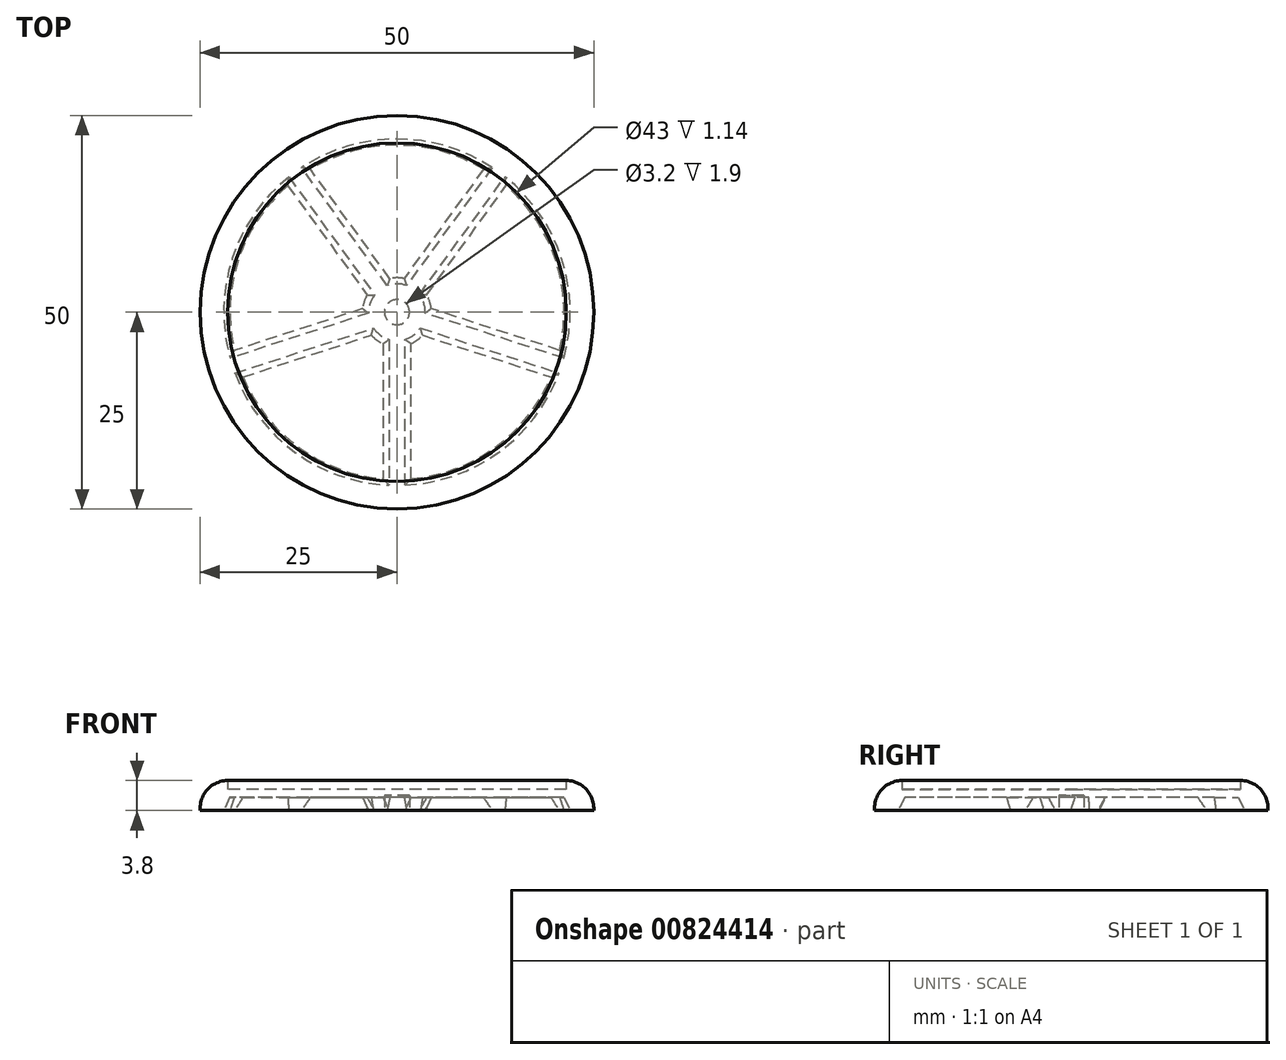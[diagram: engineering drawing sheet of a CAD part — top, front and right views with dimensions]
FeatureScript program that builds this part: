
annotation { "Feature Type Name" : "Feature", "Feature Type Description" : "" }
export const myFeature = defineFeature(function(context is Context, id is Id, definition is map)
    precondition{}
    {
        {
            var Q0;
            Q0=qCreatedBy(makeId("Top.planeOp"),FACE);
            var sketch = newSketch(context, id + "F0", { "sketchPlane" : qUnion([Q0])});
            skCircle(sketch, "E0", {"center": v(0, 0) * mm, "radius": 25 * mm});
            skCircle(sketch, "E1", {"center": v(0, 0) * mm, "radius": 21.5 * mm});
            skSolve(sketch);
        }
        {
            var Q0;
            Q0=makeQuery(id+"F0.imprint","IMPRINT",FACE,{"disambiguationData":[TD([[makeQuery(id+"F0.imprint","IMPRINT",EDGE,{"derivedFrom":sQuery(id+"F0.wireOp",EDGE,"E0")}),1.0]])]});
            extrude(context, id + "F1", {"entities" : qUnion([Q0]), "depth" : 3.8 * mm, "offsetDistance" : 25 * mm});
        }
        {
            var Q0;
            Q0=makeQuery(id+"F0.imprint","IMPRINT",FACE,{"disambiguationData":[TD([[makeQuery(id+"F0.imprint","IMPRINT",EDGE,{"derivedFrom":sQuery(id+"F0.wireOp",EDGE,"E1")}),1.0]])]});
            var Q1;
            Q1=makeQuery(id+"F1.opExtrude","CAP_FACE",FACE,{"disambiguationData":[OSD([sQuery(id+"F0.wireOp",EDGE,"E0"),sQuery(id+"F0.wireOp",EDGE,"E1")])],"isStart":false});
            extrude(context, id + "F2", {"entities" : qUnion([Q0]), "operationType" : NewBodyOperationType.ADD, "endBound" : BoundingType.UP_TO_SURFACE, "depth" : 25 * mm, "endBoundEntityFace" : qUnion([Q1]), "hasOffset" : true, "offsetDistance" : 1.14 * mm});
        }
        {
            var Q0;
            Q0=makeQuery(id+"F1.opExtrude","CAP_EDGE",EDGE,{"disambiguationData":[OSD([sQuery(id+"F0.wireOp",EDGE,"E0")])],"isStart":false});
            fillet(context, id + "F3", {"entities" : qUnion([Q0]), "radius" : 3.5 * mm, "tangentPropagation" : true, "allowEdgeOverflow" : false});
        }
        {
            var Q0;
            Q0=makeQuery(id+"F0.imprint","IMPRINT",FACE,{"disambiguationData":[TD([[makeQuery(id+"F0.imprint","IMPRINT",EDGE,{"derivedFrom":sQuery(id+"F0.wireOp",EDGE,"E1")}),1.0]])]});
            var sketch = newSketch(context, id + "F4", { "sketchPlane" : qUnion([Q0])});
            skCircle(sketch, "E2", {"center": v(0, 0) * mm, "radius": 1.6 * mm});
            skCircle(sketch, "E3", {"center": v(0, 0) * mm, "radius": 3.6 * mm});
            skCircle(sketch, "E4", {"center": v(0, 0) * mm, "radius": 22 * mm});
            skLineSegment(sketch, "E5", {"start": v(-1, -3.46) * mm, "end": v(-1, -21.98) * mm});
            skLineSegment(sketch, "E6", {"start": v(1, -3.46) * mm, "end": v(1, -21.98) * mm});
            skLineSegment(sketch, "E7.1.0", {"start": v(2.98, -2.02) * mm, "end": v(20.6, -7.74) * mm});
            skLineSegment(sketch, "E7.1.1", {"start": v(3.6, -0.12) * mm, "end": v(21.21, -5.84) * mm});
            skLineSegment(sketch, "E7.2.0", {"start": v(2.84, 2.21) * mm, "end": v(13.73, 17.2) * mm});
            skLineSegment(sketch, "E7.2.1", {"start": v(1.22, 3.39) * mm, "end": v(12.1, 18.37) * mm});
            skLineSegment(sketch, "E7.3.0", {"start": v(-1.22, 3.39) * mm, "end": v(-12.1, 18.37) * mm});
            skLineSegment(sketch, "E7.3.1", {"start": v(-2.84, 2.21) * mm, "end": v(-13.73, 17.2) * mm});
            skLineSegment(sketch, "E7.4.0", {"start": v(-3.6, -0.12) * mm, "end": v(-21.21, -5.84) * mm});
            skLineSegment(sketch, "E7.4.1", {"start": v(-2.98, -2.02) * mm, "end": v(-20.6, -7.74) * mm});
            skSolve(sketch);
        }
        {
            var Q0;
            Q0=makeQuery(id+"F4.imprint","IMPRINT",FACE,{"disambiguationData":[TD([[makeQuery(id+"F4.imprint","IMPRINT",EDGE,{"derivedFrom":sQuery(id+"F4.wireOp",EDGE,"E2")}),1.0]])]});
            extrude(context, id + "F5", {"entities" : qUnion([Q0]), "operationType" : NewBodyOperationType.REMOVE, "depth" : 1.9 * mm, "offsetDistance" : 25 * mm});
        }
        {
            var Q0;
            {var subQ0=sQuery(id+"F4.wireOp",EDGE,"E5");var subQ1=sQuery(id+"F4.wireOp",EDGE,"E3");var subQ2=makeQuery(id+"F4.imprint","INTERSECT",VERTEX,{"derivedFrom":[subQ1,subQ0]});Q0=makeQuery(id+"F4.imprint","IMPRINT",FACE,{"disambiguationData":[TD([[makeQuery(id+"F4.imprint","IMPRINT",EDGE,{"disambiguationData":[TD([[subQ2,1.0]])],"derivedFrom":subQ1}),-1.0]])]});}
            var Q1;
            {var subQ0=sQuery(id+"F4.wireOp",EDGE,"E5");var subQ1=sQuery(id+"F4.wireOp",EDGE,"E4");var subQ2=makeQuery(id+"F4.imprint","INTERSECT",VERTEX,{"derivedFrom":[subQ1,subQ0]});Q1=makeQuery(id+"F4.imprint","IMPRINT",FACE,{"disambiguationData":[TD([[makeQuery(id+"F4.imprint","IMPRINT",EDGE,{"disambiguationData":[TD([[subQ2,1.0]])],"derivedFrom":subQ1}),1.0]])]});}
            var Q2;
            {var subQ0=sQuery(id+"F4.wireOp",EDGE,"E6");var subQ1=sQuery(id+"F4.wireOp",EDGE,"E3");var subQ2=makeQuery(id+"F4.imprint","INTERSECT",VERTEX,{"derivedFrom":[subQ1,subQ0]});Q2=makeQuery(id+"F4.imprint","IMPRINT",FACE,{"disambiguationData":[TD([[makeQuery(id+"F4.imprint","IMPRINT",EDGE,{"disambiguationData":[TD([[subQ2,-1.0]])],"derivedFrom":subQ1}),-1.0]])]});}
            var Q3;
            {var subQ0=sQuery(id+"F4.wireOp",EDGE,"E6");var subQ1=sQuery(id+"F4.wireOp",EDGE,"E4");var subQ2=makeQuery(id+"F4.imprint","INTERSECT",VERTEX,{"derivedFrom":[subQ1,subQ0]});Q3=makeQuery(id+"F4.imprint","IMPRINT",FACE,{"disambiguationData":[TD([[makeQuery(id+"F4.imprint","IMPRINT",EDGE,{"disambiguationData":[TD([[subQ2,-1.0]])],"derivedFrom":subQ1}),1.0]])]});}
            var Q4;
            {var subQ0=sQuery(id+"F4.wireOp",EDGE,"E7.1.1");var subQ1=sQuery(id+"F4.wireOp",EDGE,"E3");var subQ2=makeQuery(id+"F4.imprint","INTERSECT",VERTEX,{"derivedFrom":[subQ1,subQ0]});Q4=makeQuery(id+"F4.imprint","IMPRINT",FACE,{"disambiguationData":[TD([[makeQuery(id+"F4.imprint","IMPRINT",EDGE,{"disambiguationData":[TD([[subQ2,-1.0]])],"derivedFrom":subQ1}),-1.0]])]});}
            var Q5;
            {var subQ0=sQuery(id+"F4.wireOp",EDGE,"E7.1.1");var subQ1=sQuery(id+"F4.wireOp",EDGE,"E4");var subQ2=makeQuery(id+"F4.imprint","INTERSECT",VERTEX,{"derivedFrom":[subQ1,subQ0]});Q5=makeQuery(id+"F4.imprint","IMPRINT",FACE,{"disambiguationData":[TD([[makeQuery(id+"F4.imprint","IMPRINT",EDGE,{"disambiguationData":[TD([[subQ2,-1.0]])],"derivedFrom":subQ1}),1.0]])]});}
            var Q6;
            {var subQ0=sQuery(id+"F4.wireOp",EDGE,"E7.2.1");var subQ1=sQuery(id+"F4.wireOp",EDGE,"E3");var subQ2=makeQuery(id+"F4.imprint","INTERSECT",VERTEX,{"derivedFrom":[subQ1,subQ0]});Q6=makeQuery(id+"F4.imprint","IMPRINT",FACE,{"disambiguationData":[TD([[makeQuery(id+"F4.imprint","IMPRINT",EDGE,{"disambiguationData":[TD([[subQ2,-1.0]])],"derivedFrom":subQ1}),-1.0]])]});}
            var Q7;
            {var subQ0=sQuery(id+"F4.wireOp",EDGE,"E7.2.1");var subQ1=sQuery(id+"F4.wireOp",EDGE,"E4");var subQ2=makeQuery(id+"F4.imprint","INTERSECT",VERTEX,{"derivedFrom":[subQ1,subQ0]});Q7=makeQuery(id+"F4.imprint","IMPRINT",FACE,{"disambiguationData":[TD([[makeQuery(id+"F4.imprint","IMPRINT",EDGE,{"disambiguationData":[TD([[subQ2,-1.0]])],"derivedFrom":subQ1}),1.0]])]});}
            var Q8;
            {var subQ0=sQuery(id+"F4.wireOp",EDGE,"E7.3.1");var subQ1=sQuery(id+"F4.wireOp",EDGE,"E3");var subQ2=makeQuery(id+"F4.imprint","INTERSECT",VERTEX,{"derivedFrom":[subQ1,subQ0]});Q8=makeQuery(id+"F4.imprint","IMPRINT",FACE,{"disambiguationData":[TD([[makeQuery(id+"F4.imprint","IMPRINT",EDGE,{"disambiguationData":[TD([[subQ2,-1.0]])],"derivedFrom":subQ1}),-1.0]])]});}
            var Q9;
            {var subQ0=sQuery(id+"F4.wireOp",EDGE,"E7.3.1");var subQ1=sQuery(id+"F4.wireOp",EDGE,"E4");var subQ2=makeQuery(id+"F4.imprint","INTERSECT",VERTEX,{"derivedFrom":[subQ1,subQ0]});Q9=makeQuery(id+"F4.imprint","IMPRINT",FACE,{"disambiguationData":[TD([[makeQuery(id+"F4.imprint","IMPRINT",EDGE,{"disambiguationData":[TD([[subQ2,-1.0]])],"derivedFrom":subQ1}),1.0]])]});}
            var Q10;
            Q10=makeQuery(id+"F2.opExtrude","CAP_FACE",FACE,{"disambiguationData":[OSD([sQuery(id+"F0.wireOp",EDGE,"E0"),sQuery(id+"F0.wireOp",EDGE,"E1")])],"isStart":false});
            extrude(context, id + "F6", {"entities" : qUnion([Q0, Q1, Q2, Q3, Q4, Q5, Q6, Q7, Q8, Q9]), "operationType" : NewBodyOperationType.REMOVE, "endBound" : BoundingType.UP_TO_SURFACE, "depth" : 25 * mm, "endBoundEntityFace" : qUnion([Q10]), "hasOffset" : true, "offsetDistance" : 1 * mm, "hasDraft" : true, "draftAngle" : 25 * degree, "draftPullDirection" : true});
        }
    });
